# Revit family: Access_Door-Removable_Door-Cendrex-Plastic-RPL
name_source: partatom
category: Specialty Equipment
revit_build: Autodesk Revit Architecture 2013 (Build: 20130531_2115(x64)
units: mm (PartAtom-declared; Revit-internal decimal feet)

## types (4) — shared parameters
Assembly Code = C1020700
Available Options = http://cendrex.com
Cendrex LEED Ready Program = http://www.cendrex.com
Construction Material = Plastic - Cendrex - High Impact ABS
Default Elevation = 0"
Description = Removable plastic access door
Finish = Metal - Cendrex - Powder Coated White
Frame Depth = 5/8"
Manufacturer = Cendrex
Model = RPL
Product Documentation Link = http://cendrex.com
Product Page URL = http://cendrex.com
URL = http://www.cendrex.com

## per-type parameters (varying)
| type | DH | DW | Door Height | Door Width | FH | FW | Frame Height | Frame Width |
| 6"x9" | 9" | 6" | 9" | 6" | 11 1/4" | 8 1/4" | 11 1/4" | 8 1/4" |
| 8"x8" | 8" | 8" | 8" | 8" | 10 1/4" | 10 1/4" | 10 1/4" | 10 1/4" |
| 14"x14" | 13 3/4" | 13 3/4" | 13 3/4" | 13 3/4" | 17" | 17" | 17" | 17" |
| 14"x29" | 29" | 13 3/4" | 29" | 13 3/4" | 32 1/4" | 17" | 32 1/4" | 17" |

## geometry (parser evidence)
native form markers: Blend x21, Sweep x5
no freeform markers — native parametric forms only
